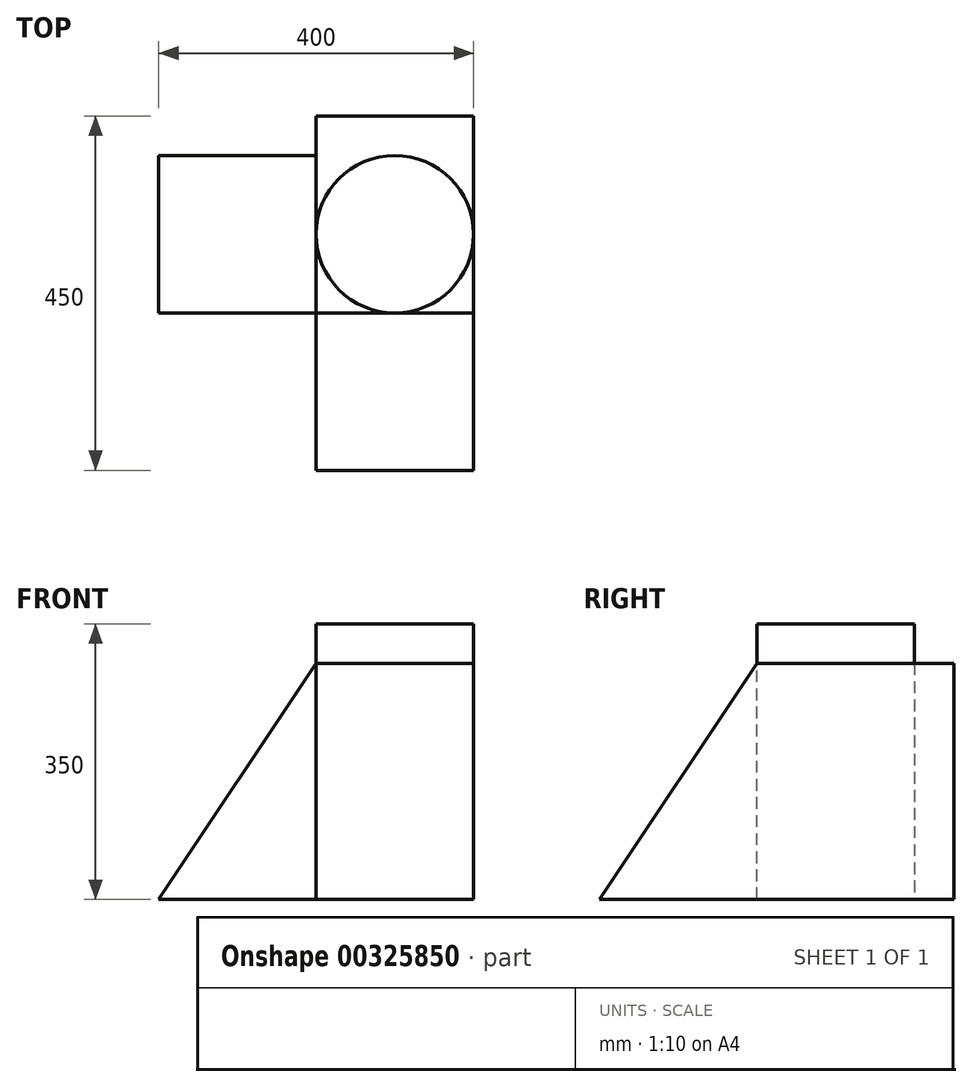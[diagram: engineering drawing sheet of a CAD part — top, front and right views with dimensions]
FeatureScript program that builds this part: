
annotation { "Feature Type Name" : "Feature", "Feature Type Description" : "" }
export const myFeature = defineFeature(function(context is Context, id is Id, definition is map)
    precondition{}
    {
        {
            var Q0;
            Q0=qCreatedBy(makeId("Right.planeOp"),FACE);
            var sketch = newSketch(context, id + "F0", { "sketchPlane" : qUnion([Q0])});
            skLineSegment(sketch, "E0.bottom", {"start": v(0, 0) * mm, "end": v(200, 0) * mm});
            skLineSegment(sketch, "E0.top", {"start": v(0, 300) * mm, "end": v(200, 300) * mm});
            skLineSegment(sketch, "E0.left", {"start": v(0, 0) * mm, "end": v(0, 300) * mm});
            skLineSegment(sketch, "E0.right", {"start": v(200, 0) * mm, "end": v(200, 300) * mm});
            skSolve(sketch);
        }
        {
            var Q0;
            Q0=makeQuery(id+"F0.imprint","IMPRINT",FACE,{"disambiguationData":[TD([[makeQuery(id+"F0.imprint","IMPRINT",EDGE,{"derivedFrom":sQuery(id+"F0.wireOp",EDGE,"E0.bottom")}),1.0]])]});
            var Q1;
            Q1=sQuery(id+"F0.wireOp",EDGE,"E0.left");
            var Q2;
            Q2=sQuery(id+"F0.wireOp",EDGE,"E0.right");
            var Q3;
            Q3=sQuery(id+"F0.wireOp",EDGE,"E0.bottom");
            var Q4;
            Q4=sQuery(id+"F0.wireOp",EDGE,"E0.top");
            extrude(context, id + "F1", {"entities" : qUnion([Q0]), "surfaceEntities" : qUnion([Q1, Q2, Q3, Q4]), "depth" : 200 * mm});
        }
        {
            var Q0;
            Q0=qCreatedBy(makeId("Right.planeOp"),FACE);
            var sketch = newSketch(context, id + "F2", { "sketchPlane" : qUnion([Q0])});
            skLineSegment(sketch, "E1", {"start": v(0, 0) * mm, "end": v(-200, 0) * mm});
            skLineSegment(sketch, "E2", {"start": v(0, 0) * mm, "end": v(0, 300) * mm});
            skLineSegment(sketch, "E3", {"start": v(0, 300) * mm, "end": v(-200, 0) * mm});
            skSolve(sketch);
        }
        {
            var Q0;
            Q0 = qSketchRegion(id + "F2", true);
            extrude(context, id + "F3", {"entities" : qUnion([Q0]), "operationType" : NewBodyOperationType.ADD, "depth" : 200 * mm});
        }
        {
            var Q0;
            Q0=makeQuery(id+"F1.opExtrude","SWEPT_FACE",FACE,{"disambiguationData":[OSD([sQuery(id+"F0.wireOp",EDGE,"E0.top")])]});
            var sketch = newSketch(context, id + "F4", { "sketchPlane" : qUnion([Q0])});
            skCircle(sketch, "E4", {"center": v(100, 100) * mm, "radius": 100 * mm});
            skPoint(sketch, "E4.centerSnap0", {"position": v(0, 100) * mm});
            skPoint(sketch, "E4.centerSnap1", {"position": v(100, 200) * mm});
            skSolve(sketch);
        }
        {
            var Q0;
            Q0 = qSketchRegion(id + "F4", true);
            extrude(context, id + "F5", {"entities" : qUnion([Q0]), "operationType" : NewBodyOperationType.ADD, "depth" : 50 * mm});
        }
        {
            var Q0;
            Q0=qCreatedBy(makeId("Front.planeOp"),FACE);
            var sketch = newSketch(context, id + "F6", { "sketchPlane" : qUnion([Q0])});
            skLineSegment(sketch, "E5", {"start": v(0, 0) * mm, "end": v(-200, 0) * mm});
            skLineSegment(sketch, "E6", {"start": v(0, 0) * mm, "end": v(0, 300) * mm});
            skLineSegment(sketch, "E7", {"start": v(0, 300) * mm, "end": v(-200, 0) * mm});
            skSolve(sketch);
        }
        {
            var Q0;
            Q0 = qSketchRegion(id + "F6", true);
            extrude(context, id + "F7", {"entities" : qUnion([Q0]), "operationType" : NewBodyOperationType.ADD, "oppositeDirection" : true, "depth" : 200 * mm});
        }
        {
            var Q0;
            Q0=makeQuery(id+"F7.boolean.opBoolean","MERGE",FACE,{"derivedFrom":[makeQuery(id+"F1.opExtrude","SWEPT_FACE",FACE,{"disambiguationData":[OSD([sQuery(id+"F0.wireOp",EDGE,"E0.right")])]}),makeQuery(id+"F7.opExtrude","CAP_FACE",FACE,{"disambiguationData":[OSD([sQuery(id+"F6.wireOp",EDGE,"E5"),sQuery(id+"F6.wireOp",EDGE,"E6"),sQuery(id+"F6.wireOp",EDGE,"E7")])],"isStart":false})]});
            var sketch = newSketch(context, id + "F8", { "sketchPlane" : qUnion([Q0])});
            skLineSegment(sketch, "E8.bottom", {"start": v(-200, 300) * mm, "end": v(0, 300) * mm});
            skLineSegment(sketch, "E8.top", {"start": v(-200, 0) * mm, "end": v(0, 0) * mm});
            skLineSegment(sketch, "E8.left", {"start": v(-200, 300) * mm, "end": v(-200, 0) * mm});
            skLineSegment(sketch, "E8.right", {"start": v(0, 300) * mm, "end": v(0, 0) * mm});
            skSolve(sketch);
        }
        {
            var Q0;
            Q0=makeQuery(id+"F8.imprint","IMPRINT",FACE,{"disambiguationData":[TD([[makeQuery(id+"F8.imprint","IMPRINT",EDGE,{"derivedFrom":sQuery(id+"F8.wireOp",EDGE,"E8.top")}),1.0]])]});
            extrude(context, id + "F9", {"entities" : qUnion([Q0]), "operationType" : NewBodyOperationType.ADD, "depth" : 50 * mm});
        }
    });
